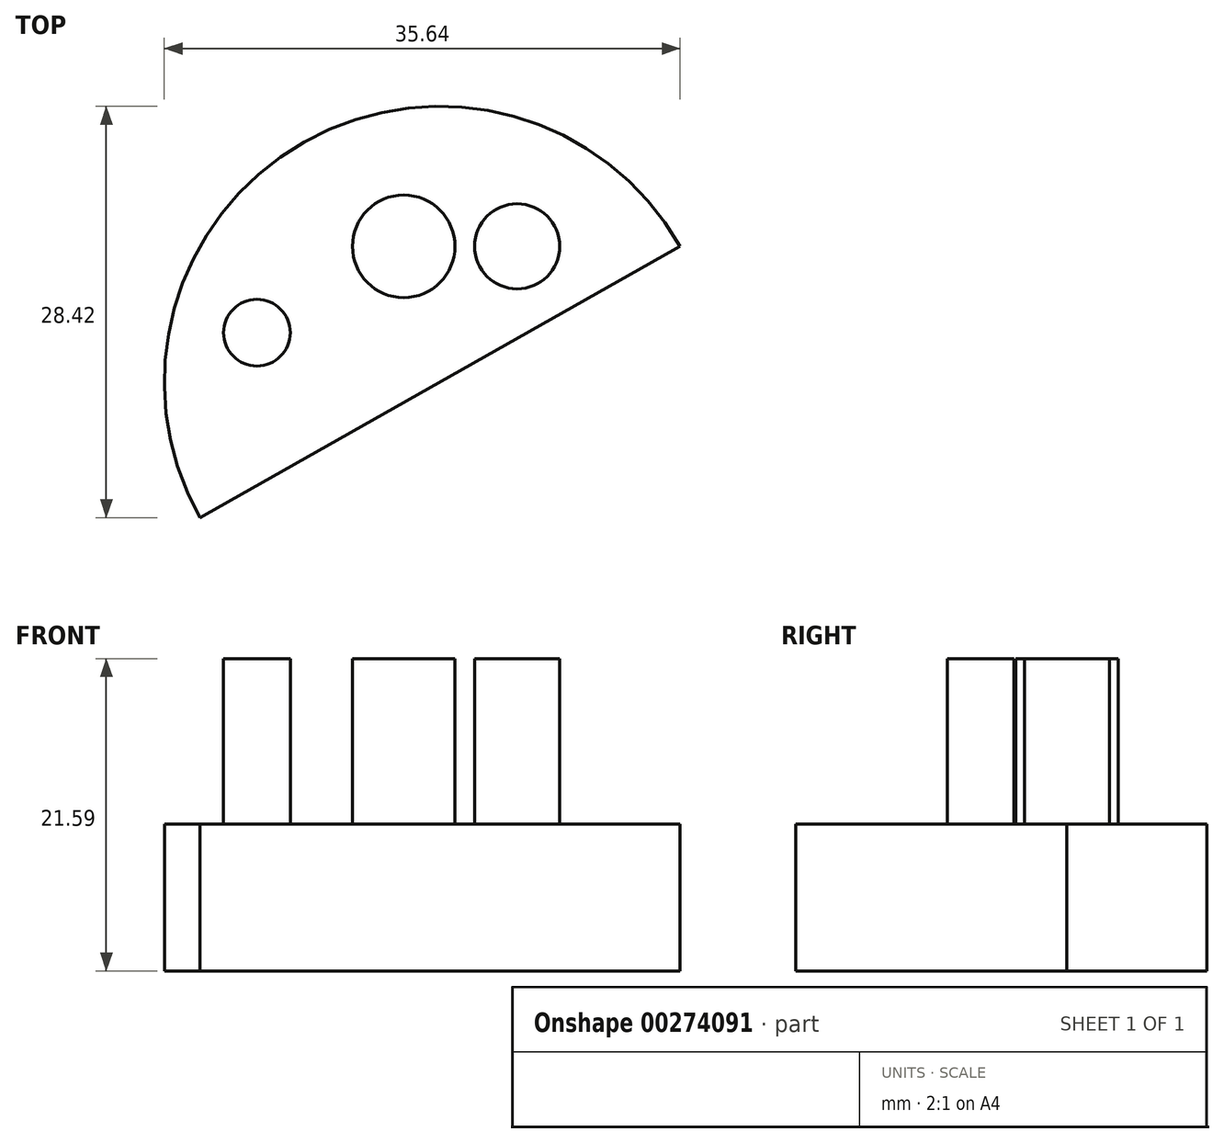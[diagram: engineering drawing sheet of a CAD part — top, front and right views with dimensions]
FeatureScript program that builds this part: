
annotation { "Feature Type Name" : "Feature", "Feature Type Description" : "" }
export const myFeature = defineFeature(function(context is Context, id is Id, definition is map)
    precondition{}
    {
        {
            var Q0;
            Q0=qCreatedBy(makeId("Top.planeOp"),FACE);
            var sketch = newSketch(context, id + "F0", { "sketchPlane" : qUnion([Q0])});
            skLineSegment(sketch, "E0", {"start": v(-31.31, 28.94) * mm, "end": v(1.86, 47.69) * mm});
            skPoint(sketch, "E1", {"position": v(-14.73, 38.31) * mm});
            skArc(sketch, "E2", {"start": v(-31.31, 28.94) * mm, "mid": v(-24.1, 54.9) * mm, "end": v(1.86, 47.69) * mm});
            skSolve(sketch);
        }
        {
            var Q0;
            Q0=makeQuery(id+"F0.imprint","IMPRINT",FACE,{"disambiguationData":[TD([[makeQuery(id+"F0.imprint","IMPRINT",EDGE,{"derivedFrom":sQuery(id+"F0.wireOp",EDGE,"E0")}),1.0]])]});
            extrude(context, id + "F1", {"entities" : qUnion([Q0]), "depth" : 10.16 * mm});
        }
        {
            var Q0;
            Q0=makeQuery(id+"F1.opExtrude","CAP_FACE",FACE,{"disambiguationData":[OSD([sQuery(id+"F0.wireOp",EDGE,"E0"),sQuery(id+"F0.wireOp",EDGE,"E2")])],"isStart":false});
            var sketch = newSketch(context, id + "F2", { "sketchPlane" : qUnion([Q0])});
            skCircle(sketch, "E3", {"center": v(-27.38, 41.72) * mm, "radius": 2.3 * mm});
            skCircle(sketch, "E4", {"center": v(-17.23, 47.69) * mm, "radius": 3.54 * mm});
            skCircle(sketch, "E5", {"center": v(-9.4, 47.69) * mm, "radius": 2.94 * mm});
            skSolve(sketch);
        }
        {
            var Q0;
            Q0 = qSketchRegion(id + "F2", true);
            extrude(context, id + "F3", {"entities" : qUnion([Q0]), "operationType" : NewBodyOperationType.ADD, "depth" : 11.43 * mm});
        }
    });
